# Revit family: Gleitlager T HV2, m.D., Ø20 bis Ø60mm (h=125-151mm)
name_source: partatom
category: HLS-Bauteile
units: mm (PartAtom-declared; Revit-internal decimal feet)

## family parameters
Arbeitsebenenbasiert = Ja
Beim Laden mit Abzugskörper schneiden = Nein
Bemaßung runder Anschluss = Durchmesser verwenden
Beschriftungsausrichtung beibehalten = Nein
Gemeinsam genutzt = Ja
Immer vertikal = Nein
Klassifizierung = Keine
Raumberechnungspunkt = Nein
Teiletyp = Normal

## types (9) — shared parameters
Anzahl Rohrschellen = 2
Baustoffklasse = B2
Breite Schellenband = 35 mm
Breite Unterbau = 100 mm
Dämmstärke = 6 mm  [stored 0.019685 ft]
Fabrikat = MEFA
Hersteller = MEFA
Kurztext1 = Gleitlager T 2 RS HV2 35x4
Länge Unterbau = 250 mm
Material = Stahl
Materialname = S235
Mengeneinheit = St
Schalldämmeinlage = Gummi EPDM
Sicherheitsfaktor = 1.54
Stärke Material = 8 mm  [stored 0.0262467 ft]
Stärke Schellenband = 4 mm
Verschluss = Mutter / Verschluss-Schraube
Vorgabe-Ansicht = 1219 mm
max. Höhe Unterbau = 150 mm
max. Temperaturbeständigkeit = 100 °C
min. Höhe Unterbau = 125 mm
vpe = 1

## per-type parameters (varying)
| type | Artikelnummer | EAN | Gewicht | Gewicht pro Bauteil | Kurztext2 | Nennweite DN Rohr | Rohraußendurchmesser | Schellenteil | max. Rohrachse | max. Rohraußendurchmesser | min. Rohrachse | min. Rohraußendurchmesser |
| Gleitlager T HV2, m.2 RS, m.D., Ø 20-22 (h=125-151mm) | 141bfbb0022 | 4250928461131 | 4.03 kg | 4.03 kg | 20 - 22 mm EPDM 100x250 mm fsv | 15 mm  [stored 0.0492126 ft] | 0 mm  [stored 0 ft] | TL-141S_b0030 bis 0068, m.D : mit RS Ø20-22mm m.D | 162 mm | 22 mm  [stored 0.0721785 ft] | 135 mm | 20 mm  [stored 0.0656168 ft] |
| Gleitlager T HV2, m.2 RS, m.D., Ø 25 (h=125-151mm) | 141bfbb0025 | 4250928461148 | 4.07 kg | 4.07 kg | 25 mm EPDM 100x250 mm fsv | 0 mm  [stored 0 ft] | 25 mm  [stored 0.082021 ft] | TL-141S_b0030 bis 0068, m.D : mit RS Ø25mm m.D | 164 mm | 0 mm  [stored 0 ft] | 138 mm | 0 mm  [stored 0 ft] |
| Gleitlager T HV2, m.2 RS, m.D., Ø 27-28 (h=125-151mm) | 141bfbb0028 | 4250928461155 | 4.09 kg | 4.09 kg | 27 - 28 mm EPDM 100x250 mm fsv | 20 mm  [stored 0.0656168 ft] | 0 mm  [stored 0 ft] | TL-141S_b0030 bis 0068, m.D : mit RS Ø27-28mm, m.D | 165 mm | 28 mm  [stored 0.0918635 ft] | 139 mm | 27 mm  [stored 0.0885827 ft] |
| Gleitlager T HV2, m.2 RS, m.D., Ø 32 (h=125-151mm) | 141bfbb0032 | 4250928461162 | 4.14 kg | 4.14 kg | 32 mm EPDM 100x250 mm fsv | 0 mm  [stored 0 ft] | 32 mm  [stored 0.104987 ft] | TL-141S_b0030 bis 0068, m.D : mit RS Ø32mm m.D | 167 mm | 0 mm  [stored 0 ft] | 141 mm | 0 mm  [stored 0 ft] |
| Gleitlager T HV2, m.2 RS, m.D., Ø 33-35 (h=125-151mm) | 141bfbb0035 | 4250928461179 | 4.17 kg | 4.17 kg | 33 - 35 mm EPDM 100x250 mm fsv | 25 mm  [stored 0.082021 ft] | 0 mm  [stored 0 ft] | TL-141S_b0030 bis 0068, m.D : mit RS Ø33-35mm m.D | 169 mm | 35 mm  [stored 0.114829 ft] | 142 mm | 33 mm  [stored 0.108268 ft] |
| Gleitlager T HV2, m.2 RS, m.D., Ø 40-42 (h=125-151mm) | 141bfbb0042 | 4250928461186 | 4.23 kg | 4.23 kg | 40 - 42 mm EPDM 100x250 mm fsv | 32 mm  [stored 0.104987 ft] | 0 mm  [stored 0 ft] | TL-141S_b0030 bis 0068, m.D : mit RS Ø40-42mm m.D | 172 mm | 42 mm  [stored 0.137795 ft] | 145 mm | 40 mm  [stored 0.131234 ft] |
| Gleitlager T HV2, m.2 RS, m.D., Ø 48-50 (h=125-151mm) | 141bfbb0050 | 4250928461193 | 4.30 kg | 4.30 kg | 48 - 50 mm EPDM 100x250 mm fsv | 40 mm  [stored 0.131234 ft] | 0 mm  [stored 0 ft] | TL-141S_b0030 bis 0068, m.D : mit RS Ø48-50mm m.D | 176 mm | 50 mm  [stored 0.164042 ft] | 149 mm | 48 mm  [stored 0.15748 ft] |
| Gleitlager T HV2, m.2 RS, m.D., Ø 54 (h=125-151mm) | 141bfbb0054 | 4250928461209 | 4.34 kg | 4.34 kg | 54 mm EPDM 100x250 mm fsv | 0 mm  [stored 0 ft] | 54 mm  [stored 0.177165 ft] | TL-141S_b0030 bis 0068, m.D : mit RS Ø54mm m.D | 178 mm | 0 mm  [stored 0 ft] | 152 mm | 0 mm  [stored 0 ft] |
| Gleitlager T HV2, m.2 RS, m.D., Ø 60 (h=125-151mm) | 141bfbb0060 | 4250928461216 | 4.40 kg | 4.40 kg | 60 mm EPDM 100x250 mm fsv | 50 mm  [stored 0.164042 ft] | 60 mm  [stored 0.19685 ft] | TL-141S_b0030 bis 0068, m.D : mit RS Ø60mm m.D | 181 mm | 0 mm  [stored 0 ft] | 155 mm | 0 mm  [stored 0 ft] |

note: [stored X ft] marks values corroborated as IEEE doubles in the binary element streams (Revit-internal decimal feet)

## geometry (parser evidence)
native form markers: Sweep x6
no freeform markers — native parametric forms only
